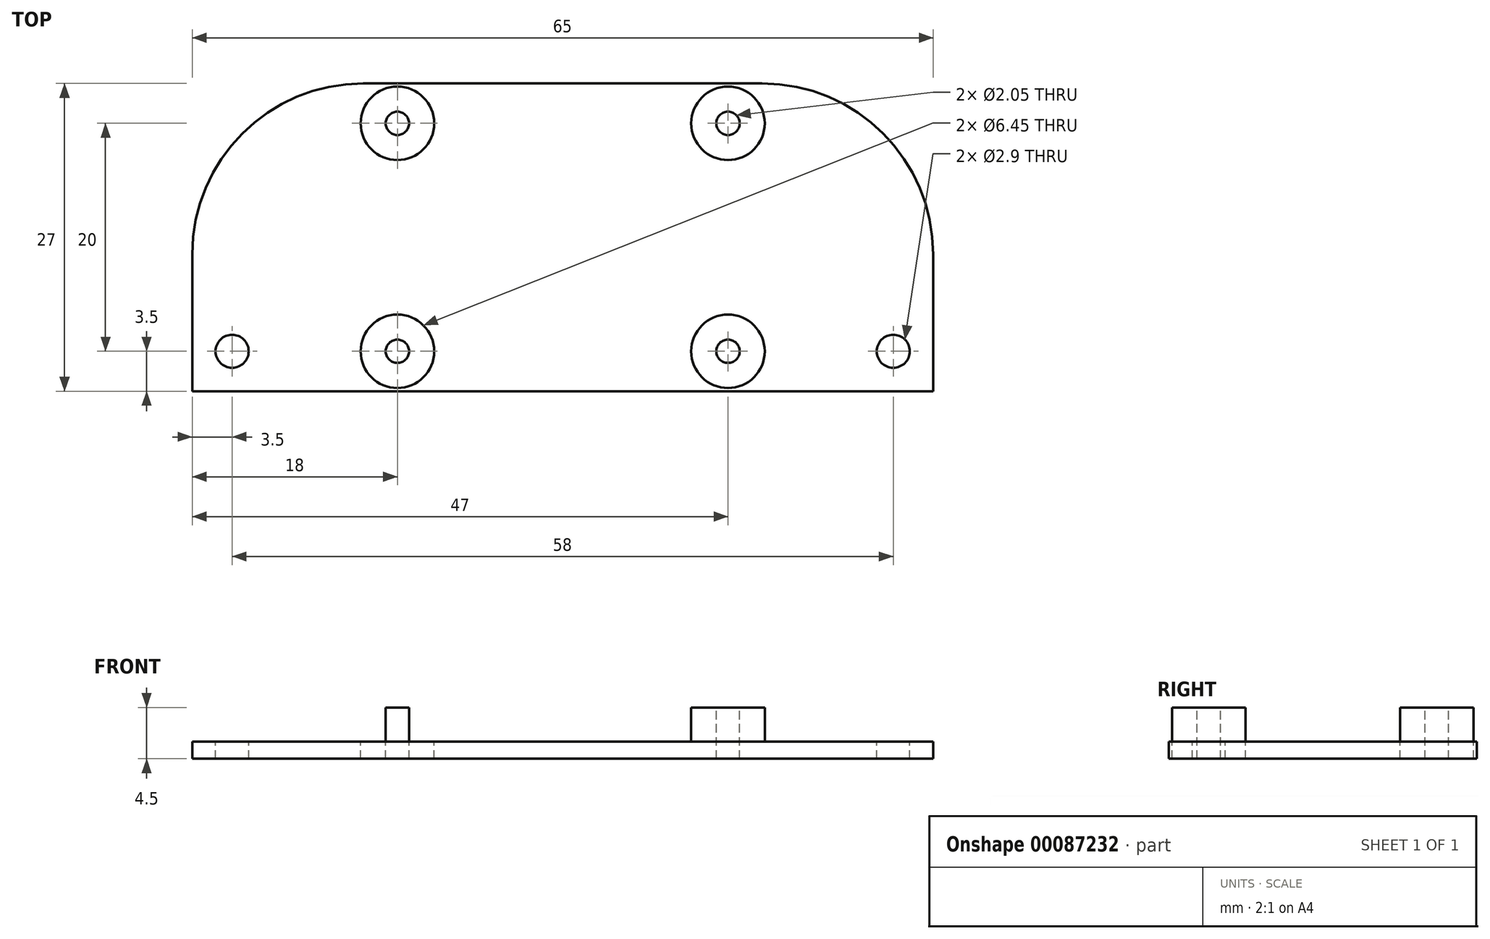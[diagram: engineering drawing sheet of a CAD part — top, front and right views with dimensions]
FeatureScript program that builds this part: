
annotation { "Feature Type Name" : "Feature", "Feature Type Description" : "" }
export const myFeature = defineFeature(function(context is Context, id is Id, definition is map)
    precondition{}
    {
        {
            var Q0;
            Q0=qCreatedBy(makeId("Top.planeOp"),FACE);
            var sketch = newSketch(context, id + "F0", { "sketchPlane" : qUnion([Q0])});
            skPoint(sketch, "E0.middle", {"position": v(0, 0) * mm});
            skCircle(sketch, "E1", {"center": v(-29, 0) * mm, "radius": 1.45 * mm});
            skCircle(sketch, "E2.MirrorC", {"center": v(29, 0) * mm, "radius": 1.45 * mm});
            skLineSegment(sketch, "E3.bottom", {"start": v(-32.5, -3.5) * mm, "end": v(32.5, -3.5) * mm});
            skLineSegment(sketch, "E3.top", {"start": v(-17.5, 23.5) * mm, "end": v(17.5, 23.5) * mm});
            skLineSegment(sketch, "E3.left", {"start": v(-32.5, -3.5) * mm, "end": v(-32.5, 8.5) * mm});
            skLineSegment(sketch, "E3.right", {"start": v(32.5, -3.5) * mm, "end": v(32.5, 8.5) * mm});
            skCircle(sketch, "E4", {"center": v(14.5, 0) * mm, "radius": 1.02 * mm});
            skCircle(sketch, "E5.MirrorC", {"center": v(-14.5, 0) * mm, "radius": 1.02 * mm});
            skCircle(sketch, "E6.0.1.0", {"center": v(-14.5, 20) * mm, "radius": 1.02 * mm});
            skCircle(sketch, "E6.0.1.1", {"center": v(14.5, 20) * mm, "radius": 1.02 * mm});
            skLineSegment(sketch, "E6.direction1", {"start": v(-14.5, 0) * mm, "end": v(10.5, 0) * mm, "construction": true});
            skLineSegment(sketch, "E6.direction2", {"start": v(-14.5, 0) * mm, "end": v(-14.5, 20) * mm, "construction": true});
            skLineSegment(sketch, "E7.direction1", {"start": v(-14.5, 0) * mm, "end": v(6.04, 0) * mm, "construction": true});
            skPoint(sketch, "E8.visualSharp", {"position": v(-32.5, 23.5) * mm});
            skArc(sketch, "E8.filletArc", {"start": v(-17.5, 23.5) * mm, "mid": v(-28.1, 19.1) * mm, "end": v(-32.5, 8.5) * mm});
            skPoint(sketch, "E9.visualSharp", {"position": v(32.5, 23.5) * mm});
            skArc(sketch, "E9.filletArc", {"start": v(32.5, 8.5) * mm, "mid": v(28.1, 19.1) * mm, "end": v(17.5, 23.5) * mm});
            skCircle(sketch, "E10.0", {"center": v(14.5, 0) * mm, "radius": 3.23 * mm});
            skCircle(sketch, "E11.0", {"center": v(14.5, 20) * mm, "radius": 3.23 * mm});
            skCircle(sketch, "E12.0", {"center": v(-14.5, 20) * mm, "radius": 3.23 * mm});
            skCircle(sketch, "E13.0", {"center": v(-14.5, 0) * mm, "radius": 3.23 * mm});
            skSolve(sketch);
        }
        {
            var Q0;
            Q0=makeQuery(id+"F0.imprint","IMPRINT",FACE,{"disambiguationData":[TD([[makeQuery(id+"F0.imprint","IMPRINT",EDGE,{"derivedFrom":sQuery(id+"F0.wireOp",EDGE,"E1")}),-1.0]])]});
            var Q1;
            Q1=makeQuery(id+"F0.imprint","IMPRINT",FACE,{"disambiguationData":[TD([[makeQuery(id+"F0.imprint","IMPRINT",EDGE,{"derivedFrom":sQuery(id+"F0.wireOp",EDGE,"E5.MirrorC")}),1.0]])]});
            var Q2;
            Q2=makeQuery(id+"F0.imprint","IMPRINT",FACE,{"disambiguationData":[TD([[makeQuery(id+"F0.imprint","IMPRINT",EDGE,{"derivedFrom":sQuery(id+"F0.wireOp",EDGE,"E6.0.1.0")}),1.0]])]});
            var Q3;
            Q3=makeQuery(id+"F0.imprint","IMPRINT",FACE,{"disambiguationData":[TD([[makeQuery(id+"F0.imprint","IMPRINT",EDGE,{"derivedFrom":sQuery(id+"F0.wireOp",EDGE,"E6.0.1.1")}),-1.0]])]});
            var Q4;
            Q4=makeQuery(id+"F0.imprint","IMPRINT",FACE,{"disambiguationData":[TD([[makeQuery(id+"F0.imprint","IMPRINT",EDGE,{"derivedFrom":sQuery(id+"F0.wireOp",EDGE,"E4")}),-1.0]])]});
            extrude(context, id + "F1", {"entities" : qUnion([Q0, Q1, Q2, Q3, Q4]), "oppositeDirection" : true, "depth" : 1.5 * mm});
        }
        {
            var Q0;
            Q0=makeQuery(id+"F0.imprint","IMPRINT",FACE,{"disambiguationData":[TD([[makeQuery(id+"F0.imprint","IMPRINT",EDGE,{"derivedFrom":sQuery(id+"F0.wireOp",EDGE,"E6.0.1.0")}),1.0]])]});
            var Q1;
            Q1=makeQuery(id+"F0.imprint","IMPRINT",FACE,{"disambiguationData":[TD([[makeQuery(id+"F0.imprint","IMPRINT",EDGE,{"derivedFrom":sQuery(id+"F0.wireOp",EDGE,"E5.MirrorC")}),1.0]])]});
            var Q2;
            Q2=makeQuery(id+"F0.imprint","IMPRINT",FACE,{"disambiguationData":[TD([[makeQuery(id+"F0.imprint","IMPRINT",EDGE,{"derivedFrom":sQuery(id+"F0.wireOp",EDGE,"E4")}),-1.0]])]});
            var Q3;
            Q3=makeQuery(id+"F0.imprint","IMPRINT",FACE,{"disambiguationData":[TD([[makeQuery(id+"F0.imprint","IMPRINT",EDGE,{"derivedFrom":sQuery(id+"F0.wireOp",EDGE,"E6.0.1.1")}),-1.0]])]});
            extrude(context, id + "F2", {"entities" : qUnion([Q0, Q1, Q2, Q3]), "operationType" : NewBodyOperationType.ADD, "depth" : 3 * mm});
        }
    });
